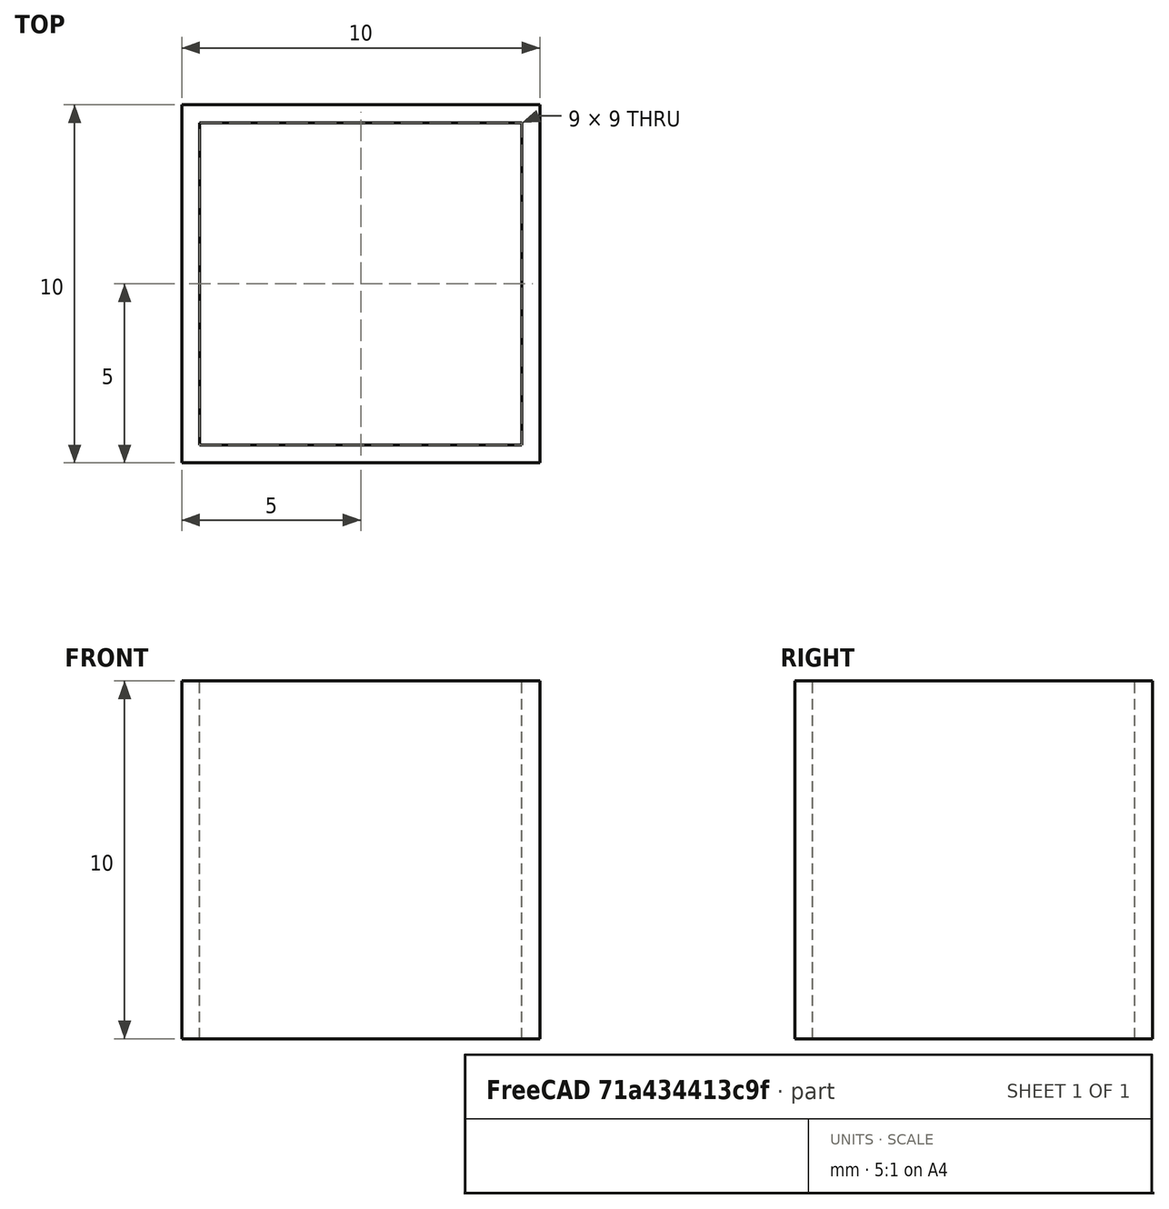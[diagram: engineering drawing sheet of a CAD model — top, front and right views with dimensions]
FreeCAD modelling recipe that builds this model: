
FCSTD DOCUMENT  (FreeCAD 0.17R11508 (Git))
Label: test_hollow_cube
License: All rights reserved
LicenseURL: http://en.wikipedia.org/wiki/All_rights_reserved
objects: Part::Box×2, Part::Cut×1, Fem::FemMeshObjectPython×1, Fem::FemSolverObjectPython×1, Fem::ConstraintDisplacement×1, App::MaterialObjectPython×1, Fem::ConstraintFixed×1, Fem::FemResultObjectPython×1, Fem::FemAnalysisPython×1
note: 3 computed .brp shape members not serialized (recipe doc carries the construction recipe); baked Part::Feature solids carry a one-line shape summary decoded from their .brp

FEATURE [Part::Box] Box  label="Cube"
  AttacherType = Attacher::AttachEngine3D
  Height = 10
  Length = 10
  Width = 10
FEATURE [Part::Box] Box001  label="Cube001"
  AttacherType = Attacher::AttachEngine3D
  Height = 10
  Length = 9
  Placement = pos=(0.5,0.5,0) rot=(0,0,1;0rad)
  Width = 9
FEATURE [Part::Cut] Cut
  Base = -> Box
  Tool = -> Box001
FEATURE [Fem::FemMeshObjectPython] FEMMeshGMSH  # FEM object (typed FeaturePython)
  Algorithm2D = 0
  Algorithm3D = 0
  CharacteristicLengthMax = 0
  CharacteristicLengthMin = 0
  CoherenceMesh = true
  ElementDimension = 0
  ElementOrder = 1
  GeometryTolerance = 1e-06
  HighOrderOptimize = false
  OptimizeNetgen = false
  OptimizeStd = true
  Part = -> Cut
  RecombineAll = false
FEATURE [Fem::FemSolverObjectPython] CalculiX  # FEM object (typed FeaturePython)
  AnalysisType = 0
  EigenmodeHighLimit = 1000000
  EigenmodeLowLimit = 0
  EigenmodesCount = 10
  GeometricalNonlinearity = 0
  IterationsControlParameterCutb = 0.25,0.5,0.75,0.85,,,1.5,
  IterationsControlParameterIter = 4,8,9,200,10,400,,200,,
  IterationsControlParameterTimeUse = false
  IterationsThermoMechMaximum = 2000
  IterationsUserDefinedIncrementations = false
  IterationsUserDefinedTimeStepLength = false
  MaterialNonlinearity = 0
  MatrixSolverType = 0
  SolverType = FemSolverCalculix
  SplitInputWriter = false
  ThermoMechSteadyState = true
  TimeEnd = 1
  TimeInitialStep = 0.01
FEATURE [Fem::ConstraintDisplacement] FemConstraintDisplacement
  NormalDirection = (0,0,1)
  Normals = (8) [(0,0,1),(0,0,1),(0,0,1),(0,0,1),(0,0,1),(0,0,1),(0,0,1),(0,0,1)]
  Points = (8) [(0,0,10),(5,0,10),(10,0,10),(0,5,10),(10,5,10),(0,10,10),(5,10,10),(10,10,10)]
  References = -> [Cut]
  rotxFix = false
  rotxFree = true
  rotyFix = false
  rotyFree = true
  rotzFix = false
  rotzFree = true
  xDisplacement = 0
  xFix = false
  xFree = true
  xRotation = 0
  yDisplacement = 0
  yFix = true
  yFree = false
  yRotation = 0
  zDisplacement = 0
  zFix = false
  zFree = true
  zRotation = 0
FEATURE [App::MaterialObjectPython] SolidMaterial  # material (typed FeaturePython)
  Category = 0
  Material = Density=1300.0 kg/m^3,+11 more (map truncated)
FEATURE [Fem::ConstraintFixed] FemConstraintFixed
  NormalDirection = (0,0,-1)
  Normals = (8) [(0,0,-1),(0,0,-1),(0,0,-1),(0,0,-1),(0,0,-1),(0,0,-1),(0,0,-1),(0,0,-1)]
  Points = (8) [(0,0,0),(5,0,0),(10,0,0),(0,5,0),(10,5,0),(0,10,0),(5,10,0),(10,10,0)]
  References = -> [Cut]
FEATURE [Fem::FemResultObjectPython] CalculiX_static_results  # FEM object (typed FeaturePython)
  DisplacementLengths = [3.14964,0,3.1496,0,0,3.14967,3.14963,3.08904,3.08907,3.08902,3.08904,0,0,0,0,0,0.537924,1.00275,1.49423,2.01566,2.57235,0.272475,0.766208,1.24474,1.751,2.29123,2.85666,3.04797,3.01019,3,3.0102,3.04801,3.08504,3.02452,3.0024,3.00241,3.02455,+2789 more]
  DisplacementVectors = (2826) [(0.288663,3,0.914819),(0,0,0),(-0.289247,3,-0.914498),(0,0,0),(0,0,0),(-0.288724,3,0.914917),(0.288621,3,-0.914792),(0.279902,3,-0.681025),+2818 more]
  Eigenmode = 0
  EigenmodeFrequency = 0
  MaxShear = [39.655,457.317,38.055,459.038,457.32,39.6658,39.6643,129.221,129.208,133.237,129.207,454.89,250.333,251.782,251.286,251.309,289.158,183.16,164.014,126.621,106.369,409.432,205.345,173.82,140.002,109.813,72.742,271.759,331.604,330.229,331.48,+2795 more]
  Mesh = -> FEMMeshGMSH
  NodeNumbers = [1,2,3,4,5,6,7,8,9,10,11,12,13,14,15,16,17,18,19,20,21,22,23,24,25,26,27,28,29,30,31,32,33,34,35,36,37,38,39,40,41,42,43,44,45,46,47,48,49,50,51,52,53,54,55,56,57,58,59,60,61,62,63,64,65,66,67,68,69,+2757 more]
  PrincipalMax = [62.8087,1322.53,15.4558,-407.62,1322.54,62.8952,16.4052,110.774,147.873,120.293,147.887,-408.225,-68.5816,-67.6566,570.528,570.559,471.549,329.488,282.148,238.06,201.477,759.596,367.451,301.984,252.871,216.025,136.667,270.065,326.013,+2797 more]
  PrincipalMed = [11.2605,509.45,-18.4119,-508.605,509.468,11.2918,-11.3569,10.86,-10.8928,11.7743,-10.8918,-510.976,-211.125,-214.669,213.39,213.413,-47.2865,0.280775,-2.50718,2.26683,3.90671,99.576,-0.56326,-0.595151,-3.43783,2.17725,-1.93437,2.39966,+2798 more]
  PrincipalMin = [-16.5014,407.892,-60.6542,-1325.7,407.897,-16.4364,-62.9234,-147.667,-110.544,-146.181,-110.526,-1318,-569.248,-571.22,67.9551,67.9414,-106.766,-36.8326,-45.881,-15.1829,-11.2602,-59.2673,-43.2393,-45.6562,-27.1333,-3.60181,-8.81732,+2799 more]
  ResultType = FemResultMechanical
  Stats = [-0.289247,-5.51356e-05,0.288663,0,1.35787,3,-0.914792,0.000262214,0.914917,0,1.39357,3.14967,21.4871,361.549,871.981,-580.306,203.681,1332.19,-690.017,-0.207736,688.614,-1336.42,-203.605,580.708,10.9993,203.643,459.038,0,0,0]
  StrainVectors = (2826) [(-0.00449514,-0.00585766,0.0147811),(-0.0284926,-0.0266078,0.227398),(0.00242735,0.00443105,-0.0117515),(0.0283209,0.0272282,-0.228004),+2822 more]
  StressValues = [69.7066,868.321,66.0461,871.981,868.321,69.7325,69.724,225.727,225.739,232.093,225.738,863.004,446.787,448.508,447.928,447.961,550.989,349.246,308.636,244.984,205.574,752.129,391.102,327.443,268.941,216.795,142.167,470.719,574.448,571.974,+2796 more]
  StressVectors = (2826) [(3.20742,-0.439313,54.7997),(516.647,521.692,1201.53),(-10.3413,-4.97845,-48.2906),(-517.648,-520.573,-1203.7),(516.657,521.715,1201.53),+2821 more]
  Time = 0
FEATURE [Fem::FemAnalysisPython] Analysis  # FEM object (typed FeaturePython)
  Member = -> [CalculiX,FEMMeshGMSH,FemConstraintDisplacement,SolidMaterial,FemConstraintFixed,CalculiX_static_results]
